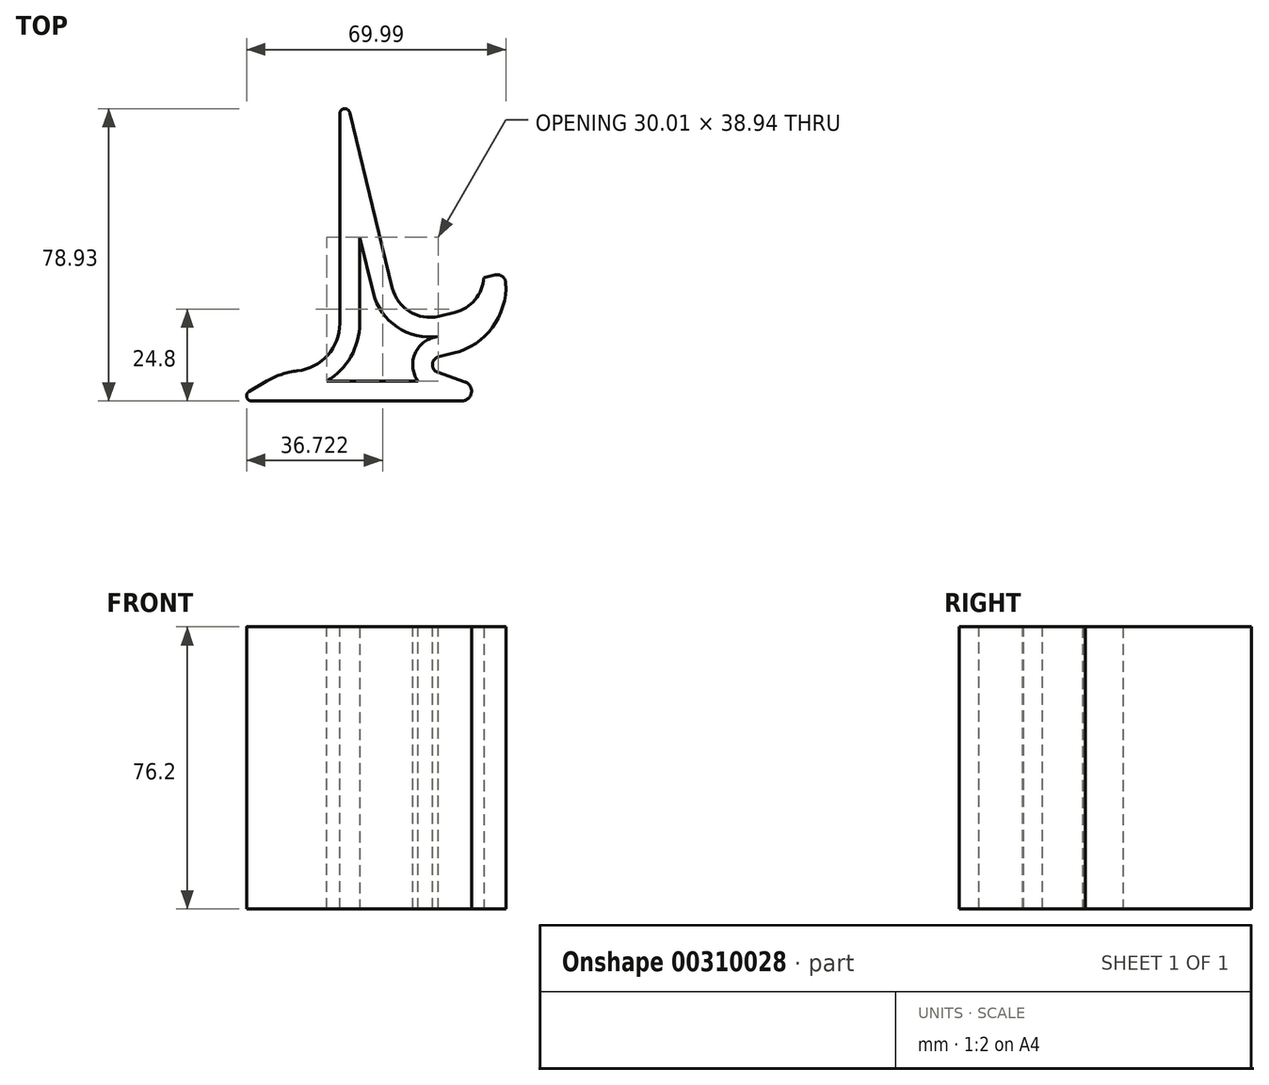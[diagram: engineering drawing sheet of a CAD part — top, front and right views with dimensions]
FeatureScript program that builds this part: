
annotation { "Feature Type Name" : "Feature", "Feature Type Description" : "" }
export const myFeature = defineFeature(function(context is Context, id is Id, definition is map)
    precondition{}
    {
        {
            var Q0;
            Q0=qCreatedBy(makeId("Top.planeOp"),FACE);
            var sketch = newSketch(context, id + "F0", { "sketchPlane" : qUnion([Q0])});
            skLineSegment(sketch, "E0", {"start": v(-47.03, 62.97) * mm, "end": v(-23.99, -31.72) * mm});
            skLineSegment(sketch, "E1", {"start": v(-23.99, -31.72) * mm, "end": v(0, -25.88) * mm});
            skLineSegment(sketch, "E2", {"start": v(0, -25.88) * mm, "end": v(-1.72, -18.81) * mm});
            skLineSegment(sketch, "E3", {"start": v(-1.72, -18.81) * mm, "end": v(3.78, -17.48) * mm});
            skLineSegment(sketch, "E4", {"start": v(3.78, -17.48) * mm, "end": v(8, -34.84) * mm});
            skLineSegment(sketch, "E5", {"start": v(8, -34.84) * mm, "end": v(-21.2, -41.95) * mm});
            skLineSegment(sketch, "E6", {"start": v(-21.2, -41.95) * mm, "end": v(7.9, -52.12) * mm});
            skLineSegment(sketch, "E7", {"start": v(7.9, -52.12) * mm, "end": v(-69.43, -52.12) * mm});
            skLineSegment(sketch, "E8", {"start": v(-69.43, -52.12) * mm, "end": v(-55.86, -44.07) * mm});
            skLineSegment(sketch, "E9", {"start": v(-55.86, -44.07) * mm, "end": v(-55.86, 62.97) * mm});
            skLineSegment(sketch, "E10", {"start": v(-55.86, 62.97) * mm, "end": v(-47.03, 62.97) * mm});
            skSolve(sketch);
        }
        {
            var Q0;
            Q0=makeQuery(id+"F0.imprint","IMPRINT",FACE,{"disambiguationData":[TD([[makeQuery(id+"F0.imprint","IMPRINT",EDGE,{"derivedFrom":sQuery(id+"F0.wireOp",EDGE,"E0")}),-1.0]])]});
            extrude(context, id + "F1", {"entities" : qUnion([Q0]), "depth" : 76.2 * mm});
        }
        {
            var Q0;
            Q0=makeQuery(id+"F1.opExtrude","SWEPT_FACE",FACE,{"disambiguationData":[OSD([sQuery(id+"F0.wireOp",EDGE,"E9")])]});
            extrude(context, id + "F2", {"entities" : qUnion([Q0]), "operationType" : NewBodyOperationType.REMOVE, "oppositeDirection" : true, "depth" : 15.24 * mm});
        }
        {
            var Q0;
            Q0=makeQuery(id+"F2.boolean.opBoolean","COPY",EDGE,{"derivedFrom":makeQuery(id+"F2.opExtrude","CAP_EDGE",EDGE,{"disambiguationData":[OSD([sQuery(id+"F0.wireOp",EDGE,"E8"),sQuery(id+"F0.wireOp",EDGE,"E9")])],"isStart":false})});
            fillet(context, id + "F3", {"entities" : qUnion([Q0]), "radius" : 12.88 * mm, "tangentPropagation" : true, "allowEdgeOverflow" : false});
        }
        {
            var Q0;
            {var subQ0=sQuery(id+"F0.wireOp",EDGE,"E9");var subQ1=sQuery(id+"F0.wireOp",EDGE,"E8");Q0=makeQuery(id+"F2.boolean.opBoolean","MERGE",EDGE,{"derivedFrom":[makeQuery(id+"F1.opExtrude","SWEPT_EDGE",EDGE,{"disambiguationData":[OSD([subQ1,subQ0])]}),makeQuery(id+"F2.opExtrude","CAP_EDGE",EDGE,{"disambiguationData":[OSD([subQ1,subQ0])],"isStart":true})]});}
            fillet(context, id + "F4", {"entities" : qUnion([Q0]), "radius" : 20.62 * mm, "tangentPropagation" : true, "allowEdgeOverflow" : false});
        }
        {
            var Q0;
            Q0=makeQuery(id+"F1.opExtrude","SWEPT_EDGE",EDGE,{"disambiguationData":[OSD([sQuery(id+"F0.wireOp",EDGE,"E7"),sQuery(id+"F0.wireOp",EDGE,"E8")])]});
            fillet(context, id + "F5", {"entities" : qUnion([Q0]), "radius" : 1.37 * mm, "tangentPropagation" : true, "allowEdgeOverflow" : false});
        }
        {
            var Q0;
            Q0=makeQuery(id+"F1.opExtrude","SWEPT_EDGE",EDGE,{"disambiguationData":[OSD([sQuery(id+"F0.wireOp",EDGE,"E5"),sQuery(id+"F0.wireOp",EDGE,"E6")])]});
            fillet(context, id + "F6", {"entities" : qUnion([Q0]), "radius" : 2.2 * mm, "tangentPropagation" : true, "allowEdgeOverflow" : false});
        }
        {
            var Q0;
            Q0=makeQuery(id+"F1.opExtrude","SWEPT_EDGE",EDGE,{"disambiguationData":[OSD([sQuery(id+"F0.wireOp",EDGE,"E6"),sQuery(id+"F0.wireOp",EDGE,"E7")])]});
            fillet(context, id + "F7", {"entities" : qUnion([Q0]), "radius" : 2.65 * mm, "tangentPropagation" : true, "allowEdgeOverflow" : false});
        }
        {
            var Q0;
            Q0=makeQuery(id+"F2.boolean.opBoolean","INTERSECT",EDGE,{"derivedFrom":[makeQuery(id+"F1.opExtrude","SWEPT_FACE",FACE,{"disambiguationData":[OSD([sQuery(id+"F0.wireOp",EDGE,"E0")])]}),makeQuery(id+"F2.opExtrude","CAP_FACE",FACE,{"disambiguationData":[OSD([sQuery(id+"F0.wireOp",EDGE,"E9")])],"isStart":false})]});
            fillet(context, id + "F8", {"entities" : qUnion([Q0]), "radius" : 1.34 * mm, "tangentPropagation" : true, "allowEdgeOverflow" : false});
        }
        {
            var Q0;
            Q0=makeQuery(id+"F1.opExtrude","SWEPT_EDGE",EDGE,{"disambiguationData":[OSD([sQuery(id+"F0.wireOp",EDGE,"E0"),sQuery(id+"F0.wireOp",EDGE,"E1")])]});
            var Q1;
            Q1=makeQuery(id+"F1.opExtrude","SWEPT_EDGE",EDGE,{"disambiguationData":[OSD([sQuery(id+"F0.wireOp",EDGE,"E1"),sQuery(id+"F0.wireOp",EDGE,"E2")])]});
            fillet(context, id + "F9", {"entities" : qUnion([Q0, Q1]), "radius" : 10.42 * mm, "tangentPropagation" : true, "allowEdgeOverflow" : false});
        }
        {
            var Q0;
            Q0=makeQuery(id+"F1.opExtrude","SWEPT_EDGE",EDGE,{"disambiguationData":[OSD([sQuery(id+"F0.wireOp",EDGE,"E4"),sQuery(id+"F0.wireOp",EDGE,"E5")])]});
            fillet(context, id + "F10", {"entities" : qUnion([Q0]), "radius" : 18.4 * mm, "tangentPropagation" : true, "allowEdgeOverflow" : false});
        }
        {
            var Q0;
            Q0=makeQuery(id+"F10.opFillet","BLEND_EDGE",EDGE,{"blendedFrom":[makeQuery(id+"F1.opExtrude","SWEPT_EDGE",EDGE,{"disambiguationData":[OSD([sQuery(id+"F0.wireOp",EDGE,"E4"),sQuery(id+"F0.wireOp",EDGE,"E5")])]}),makeQuery(id+"F1.opExtrude","SWEPT_FACE",FACE,{"disambiguationData":[OSD([sQuery(id+"F0.wireOp",EDGE,"E3")])]})],"blendedInto":[makeQuery(id+"F1.opExtrude","SWEPT_FACE",FACE,{"disambiguationData":[OSD([sQuery(id+"F0.wireOp",EDGE,"E3")])]})]});
            fillet(context, id + "F11", {"entities" : qUnion([Q0]), "radius" : 2.34 * mm, "tangentPropagation" : true, "allowEdgeOverflow" : false});
        }
        {
            var Q0;
            Q0=makeQuery(id+"F1.opExtrude","CAP_FACE",FACE,{"disambiguationData":[OSD([sQuery(id+"F0.wireOp",EDGE,"E0"),sQuery(id+"F0.wireOp",EDGE,"E1"),sQuery(id+"F0.wireOp",EDGE,"E2"),sQuery(id+"F0.wireOp",EDGE,"E3"),sQuery(id+"F0.wireOp",EDGE,"E4"),sQuery(id+"F0.wireOp",EDGE,"E5"),sQuery(id+"F0.wireOp",EDGE,"E6"),sQuery(id+"F0.wireOp",EDGE,"E7"),sQuery(id+"F0.wireOp",EDGE,"E8"),sQuery(id+"F0.wireOp",EDGE,"E9"),sQuery(id+"F0.wireOp",EDGE,"E10")])],"isStart":false});
            var Q1;
            Q1=makeQuery(id+"F1.opExtrude","CAP_FACE",FACE,{"disambiguationData":[OSD([sQuery(id+"F0.wireOp",EDGE,"E0"),sQuery(id+"F0.wireOp",EDGE,"E1"),sQuery(id+"F0.wireOp",EDGE,"E2"),sQuery(id+"F0.wireOp",EDGE,"E3"),sQuery(id+"F0.wireOp",EDGE,"E4"),sQuery(id+"F0.wireOp",EDGE,"E5"),sQuery(id+"F0.wireOp",EDGE,"E6"),sQuery(id+"F0.wireOp",EDGE,"E7"),sQuery(id+"F0.wireOp",EDGE,"E8"),sQuery(id+"F0.wireOp",EDGE,"E9"),sQuery(id+"F0.wireOp",EDGE,"E10")])],"isStart":true});
            shell(context, id + "F12", {"entities" : qUnion([Q0, Q1]), "thickness" : 5.33 * mm});
        }
    });
